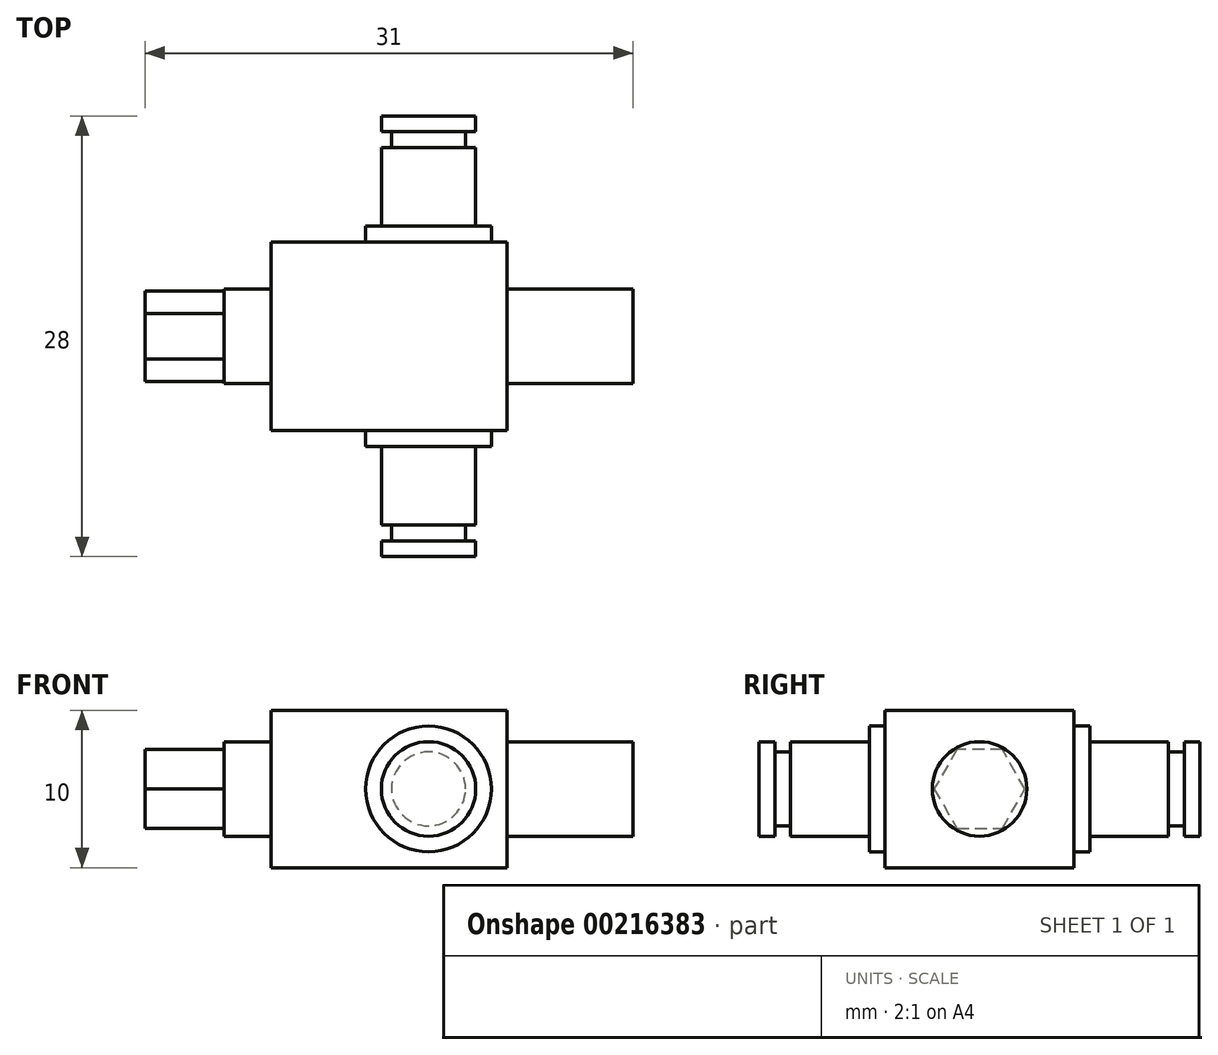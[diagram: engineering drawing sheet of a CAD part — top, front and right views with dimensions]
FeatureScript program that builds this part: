
annotation { "Feature Type Name" : "Feature", "Feature Type Description" : "" }
export const myFeature = defineFeature(function(context is Context, id is Id, definition is map)
    precondition{}
    {
        {
            var Q0;
            Q0=qCreatedBy(makeId("Top.planeOp"),FACE);
            var sketch = newSketch(context, id + "F0", { "sketchPlane" : qUnion([Q0])});
            skLineSegment(sketch, "E0", {"start": v(-10, 0) * mm, "end": v(-10, 6) * mm});
            skLineSegment(sketch, "E1", {"start": v(-10, 6) * mm, "end": v(5, 6) * mm});
            skLineSegment(sketch, "E2", {"start": v(5, 6) * mm, "end": v(5, 0) * mm});
            skLineSegment(sketch, "E3", {"start": v(5, 0) * mm, "end": v(-10, 0) * mm});
            skSolve(sketch);
        }
        {
            var Q0;
            Q0=makeQuery(id+"F0.imprint","IMPRINT",FACE,{"disambiguationData":[TD([[makeQuery(id+"F0.imprint","IMPRINT",EDGE,{"derivedFrom":sQuery(id+"F0.wireOp",EDGE,"E0")}),-1.0]])]});
            extrude(context, id + "F1", {"entities" : qUnion([Q0]), "depth" : 10 * mm, "offsetDistance" : 25 * mm});
        }
        {
            var Q0;
            Q0=qCreatedBy(makeId("Right.planeOp"),FACE);
            var sketch = newSketch(context, id + "F2", { "sketchPlane" : qUnion([Q0])});
            skLineSegment(sketch, "E4", {"start": v(6, 5) * mm, "end": v(14, 5) * mm});
            skLineSegment(sketch, "E5", {"start": v(14, 5) * mm, "end": v(14, 8) * mm});
            skLineSegment(sketch, "E6", {"start": v(14, 8) * mm, "end": v(13, 8) * mm});
            skLineSegment(sketch, "E7", {"start": v(13, 8) * mm, "end": v(13, 7.35) * mm});
            skLineSegment(sketch, "E8", {"start": v(13, 7.35) * mm, "end": v(12, 7.35) * mm});
            skLineSegment(sketch, "E9", {"start": v(12, 7.35) * mm, "end": v(12, 8) * mm});
            skLineSegment(sketch, "E10", {"start": v(12, 8) * mm, "end": v(7, 8) * mm});
            skLineSegment(sketch, "E11", {"start": v(7, 8) * mm, "end": v(7, 9) * mm});
            skLineSegment(sketch, "E12", {"start": v(7, 9) * mm, "end": v(6, 9) * mm});
            skLineSegment(sketch, "E13", {"start": v(6, 9) * mm, "end": v(6, 5) * mm});
            skSolve(sketch);
        }
        {
            var Q0;
            Q0=makeQuery(id+"F2.imprint","IMPRINT",FACE,{"disambiguationData":[TD([[makeQuery(id+"F2.imprint","IMPRINT",EDGE,{"derivedFrom":sQuery(id+"F2.wireOp",EDGE,"E4")}),1.0]])]});
            var Q1;
            Q1=sQuery(id+"F2.wireOp",EDGE,"E4");
            revolve(context, id + "F3", {"operationType" : NewBodyOperationType.ADD, "surfaceOperationType" : NewSurfaceOperationType.NEW, "entities" : qUnion([Q0]), "axis" : qUnion([Q1]), "revolveType" : RevolveType.FULL});
        }
        {
            var Q0;
            Q0=makeQuery(id+"F1.opExtrude","SWEPT_BODY",BODY,{"disambiguationData":[OSD([sQuery(id+"F0.wireOp",EDGE,"E0"),sQuery(id+"F0.wireOp",EDGE,"E1"),sQuery(id+"F0.wireOp",EDGE,"E2"),sQuery(id+"F0.wireOp",EDGE,"E3")])]});
            var Q1;
            Q1=qCreatedBy(makeId("Front.planeOp"),FACE);
            mirror(context, id + "F4", {"operationType" : NewBodyOperationType.ADD, "entities" : qUnion([Q0]), "mirrorPlane" : qUnion([Q1])});
        }
        {
            var Q0;
            Q0=makeQuery(id+"F1.opExtrude","SWEPT_FACE",FACE,{"disambiguationData":[OSD([sQuery(id+"F0.wireOp",EDGE,"E0")])]});
            var sketch = newSketch(context, id + "F5", { "sketchPlane" : qUnion([Q0])});
            skLineSegment(sketch, "E14", {"start": v(0, 10) * mm, "end": v(0, 0) * mm, "construction": true});
            skCircle(sketch, "E15", {"center": v(0, 5) * mm, "radius": 3 * mm});
            skSolve(sketch);
        }
        {
            var Q0;
            Q0=makeQuery(id+"F5.imprint","IMPRINT",FACE,{"disambiguationData":[TD([[makeQuery(id+"F5.imprint","IMPRINT",EDGE,{"derivedFrom":sQuery(id+"F5.wireOp",EDGE,"E15")}),1.0]])]});
            extrude(context, id + "F6", {"entities" : qUnion([Q0]), "operationType" : NewBodyOperationType.ADD, "depth" : 8 * mm, "offsetDistance" : 25 * mm});
        }
        {
            var Q0;
            {var subQ0=makeQuery(id+"F1.opExtrude","SWEPT_FACE",FACE,{"disambiguationData":[OSD([sQuery(id+"F0.wireOp",EDGE,"E2")])]});Q0=makeQuery(id+"F4.boolean.opBoolean","MERGE",FACE,{"derivedFrom":[subQ0,makeQuery(id+"F4.opPattern","COPY",FACE,{"derivedFrom":subQ0,"instanceName":"1"})]});}
            var sketch = newSketch(context, id + "F7", { "sketchPlane" : qUnion([Q0])});
            skLineSegment(sketch, "E16", {"start": v(0, 0) * mm, "end": v(0, 10) * mm, "construction": true});
            skCircle(sketch, "E17", {"center": v(0, 5) * mm, "radius": 3 * mm});
            skSolve(sketch);
        }
        {
            var Q0;
            Q0=makeQuery(id+"F7.imprint","IMPRINT",FACE,{"disambiguationData":[TD([[makeQuery(id+"F7.imprint","IMPRINT",EDGE,{"derivedFrom":sQuery(id+"F7.wireOp",EDGE,"E17")}),1.0]])]});
            extrude(context, id + "F8", {"entities" : qUnion([Q0]), "operationType" : NewBodyOperationType.ADD, "depth" : 8 * mm, "offsetDistance" : 25 * mm});
        }
        {
            var Q0;
            Q0=makeQuery(id+"F6.opExtrude","CAP_FACE",FACE,{"disambiguationData":[OSD([sQuery(id+"F5.wireOp",EDGE,"E15")])],"isStart":false});
            var sketch = newSketch(context, id + "F9", { "sketchPlane" : qUnion([Q0])});
            skCircle(sketch, "E18.cCircle", {"center": v(0, 5) * mm, "radius": 2.5 * mm, "construction": true});
            skLineSegment(sketch, "E18.0", {"start": v(1.44, 7.5) * mm, "end": v(2.89, 5) * mm});
            skLineSegment(sketch, "E18.1", {"start": v(2.89, 5) * mm, "end": v(1.44, 2.5) * mm});
            skLineSegment(sketch, "E18.2", {"start": v(1.44, 2.5) * mm, "end": v(-1.44, 2.5) * mm});
            skLineSegment(sketch, "E18.3", {"start": v(-1.44, 2.5) * mm, "end": v(-2.89, 5) * mm});
            skLineSegment(sketch, "E18.4", {"start": v(-2.89, 5) * mm, "end": v(-1.44, 7.5) * mm});
            skLineSegment(sketch, "E18.5", {"start": v(-1.44, 7.5) * mm, "end": v(1.44, 7.5) * mm});
            skPoint(sketch, "E18.0.midPoint", {"position": v(2.17, 6.25) * mm});
            skSolve(sketch);
        }
        {
            var Q0;
            Q0=makeQuery(id+"F9.imprint","IMPRINT",FACE,{"disambiguationData":[TD([[makeQuery(id+"F9.imprint","IMPRINT",EDGE,{"derivedFrom":sQuery(id+"F9.wireOp",EDGE,"E18.0")}),1.0]])]});
            extrude(context, id + "F10", {"entities" : qUnion([Q0]), "operationType" : NewBodyOperationType.REMOVE, "oppositeDirection" : true, "depth" : 5 * mm, "offsetDistance" : 25 * mm});
        }
    });
